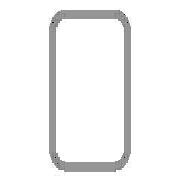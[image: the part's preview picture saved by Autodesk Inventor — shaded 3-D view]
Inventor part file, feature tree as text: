
AUTODESK INVENTOR PART (.ipt)
format: ipt  version: 2025.3 (Build 293356000, 356)  size: 133,120 bytes
history: native  units: mm (DEFAULTED — no unit token found)
features: other x4, sketch x1, plane x1
ambient origin geometry x8: Origin, YZ Plane, XZ Plane, XY Plane, X Axis, Y Axis, Z Axis, Center Point
bodies: Solid1 (feature_tree), Body (feature_tree)
feature tree (6):
  parser-record x1  (decoder bookkeeping rows leaked as tree rows — omitted from the tree; the rows remain in map.json)
  other  "Driven Length"
  other  "Start Plane"
  other  "End Plane"
  sketch  "Sketch3"  dims[d3=355.503094mm d4=0.0mm d7=6.0mm d9=40.0mm d11=80.0mm d12=3.0mm d13=-0.0mm d14=355.503094mm d15=20.0mm d16=40.0mm d17=90.0deg d18=355.503094mm]
  plane  "Work Plane3"
